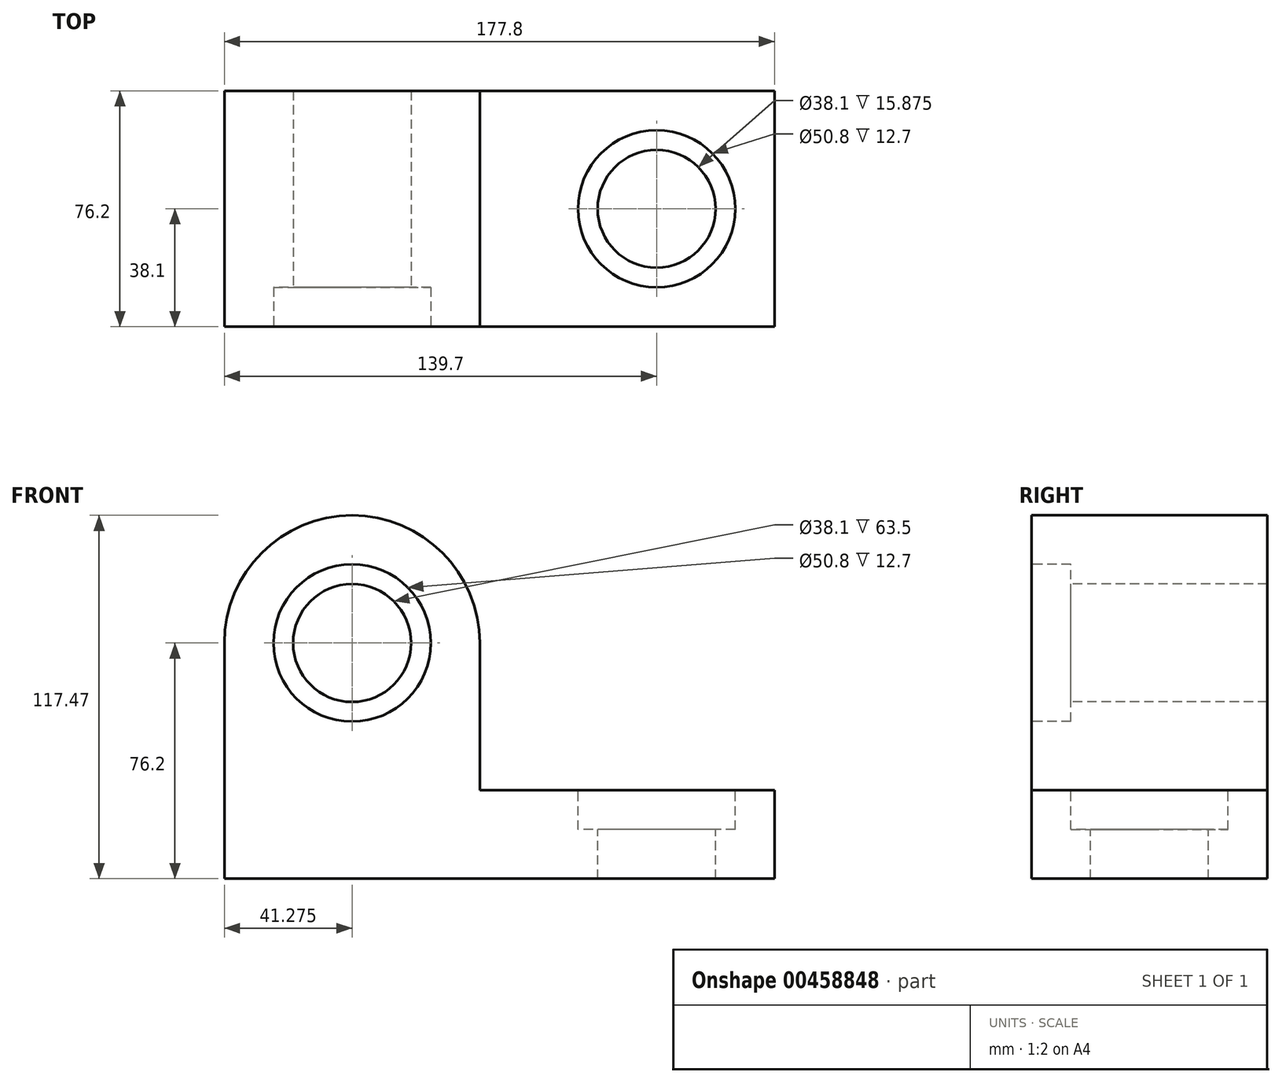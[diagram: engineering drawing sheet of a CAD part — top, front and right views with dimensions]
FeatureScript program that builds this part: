
annotation { "Feature Type Name" : "Feature", "Feature Type Description" : "" }
export const myFeature = defineFeature(function(context is Context, id is Id, definition is map)
    precondition{}
    {
        {
            var Q0;
            Q0=qCreatedBy(makeId("Front.planeOp"),FACE);
            var sketch = newSketch(context, id + "F0", { "sketchPlane" : qUnion([Q0])});
            skLineSegment(sketch, "E0", {"start": v(0, 0) * mm, "end": v(177.8, 0) * mm});
            skLineSegment(sketch, "E1", {"start": v(0, 0) * mm, "end": v(0, 76.2) * mm});
            skArc(sketch, "E2", {"start": v(0, 76.2) * mm, "mid": v(41.28, 117.48) * mm, "end": v(82.55, 76.2) * mm});
            skLineSegment(sketch, "E3", {"start": v(82.55, 76.2) * mm, "end": v(82.55, 28.57) * mm});
            skLineSegment(sketch, "E4", {"start": v(82.55, 28.57) * mm, "end": v(177.8, 28.58) * mm});
            skLineSegment(sketch, "E5", {"start": v(177.8, 28.58) * mm, "end": v(177.8, 0) * mm});
            skSolve(sketch);
        }
        {
            var Q0;
            Q0=makeQuery(id+"F0.imprint","IMPRINT",FACE,{"disambiguationData":[TD([[makeQuery(id+"F0.imprint","IMPRINT",EDGE,{"derivedFrom":sQuery(id+"F0.wireOp",EDGE,"E0")}),1.0]])]});
            extrude(context, id + "F1", {"entities" : qUnion([Q0]), "depth" : 76.2 * mm});
        }
        {
            var Q0;
            Q0=makeQuery(id+"F1.opExtrude","SWEPT_FACE",FACE,{"disambiguationData":[OSD([sQuery(id+"F0.wireOp",EDGE,"E4")])]});
            var sketch = newSketch(context, id + "F2", { "sketchPlane" : qUnion([Q0])});
            skPoint(sketch, "E6", {"position": v(139.7, -38.1) * mm});
            skSolve(sketch);
        }
        {
            var Q0;
            Q0=makeQuery(id+"F1.opExtrude","CAP_FACE",FACE,{"disambiguationData":[OSD([sQuery(id+"F0.wireOp",EDGE,"E0"),sQuery(id+"F0.wireOp",EDGE,"E1"),sQuery(id+"F0.wireOp",EDGE,"E2"),sQuery(id+"F0.wireOp",EDGE,"E3"),sQuery(id+"F0.wireOp",EDGE,"E4"),sQuery(id+"F0.wireOp",EDGE,"E5")])],"isStart":false});
            var sketch = newSketch(context, id + "F3", { "sketchPlane" : qUnion([Q0])});
            skPoint(sketch, "E7", {"position": v(41.28, 76.2) * mm});
            skSolve(sketch);
        }
        {
            var Q0;
            Q0=sQuery(id+"F3.wireOp",VERTEX,"E7");
            var Q1;
            Q1=makeQuery(id+"F1.opExtrude","SWEPT_BODY",BODY,{"disambiguationData":[OSD([sQuery(id+"F0.wireOp",EDGE,"E0"),sQuery(id+"F0.wireOp",EDGE,"E1"),sQuery(id+"F0.wireOp",EDGE,"E2"),sQuery(id+"F0.wireOp",EDGE,"E3"),sQuery(id+"F0.wireOp",EDGE,"E4"),sQuery(id+"F0.wireOp",EDGE,"E5")])]});
            hole(context, id + "F4", {"style" : HoleStyle.C_BORE, "endStyle" : HoleEndStyle.THROUGH, "holeDiameter" : 38.1 * mm, "cBoreDiameter" : 50.8 * mm, "cBoreDepth" : 12.7 * mm, "isTappedThrough" : true, "tappedDepth" : 12.7 * mm, "tapClearance" : 3, "startFromSketch" : true, "locations" : qUnion([Q0]), "scope" : qUnion([Q1])});
        }
        {
            var Q0;
            Q0=sQuery(id+"F2.wireOp",VERTEX,"E6");
            var Q1;
            Q1=makeQuery(id+"F1.opExtrude","SWEPT_BODY",BODY,{"disambiguationData":[OSD([sQuery(id+"F0.wireOp",EDGE,"E0"),sQuery(id+"F0.wireOp",EDGE,"E1"),sQuery(id+"F0.wireOp",EDGE,"E2"),sQuery(id+"F0.wireOp",EDGE,"E3"),sQuery(id+"F0.wireOp",EDGE,"E4"),sQuery(id+"F0.wireOp",EDGE,"E5")])]});
            hole(context, id + "F5", {"style" : HoleStyle.C_BORE, "endStyle" : HoleEndStyle.THROUGH, "holeDiameter" : 38.1 * mm, "cBoreDiameter" : 50.8 * mm, "cBoreDepth" : 12.7 * mm, "isTappedThrough" : true, "tappedDepth" : 12.7 * mm, "tapClearance" : 3, "startFromSketch" : true, "locations" : qUnion([Q0]), "scope" : qUnion([Q1])});
        }
    });
